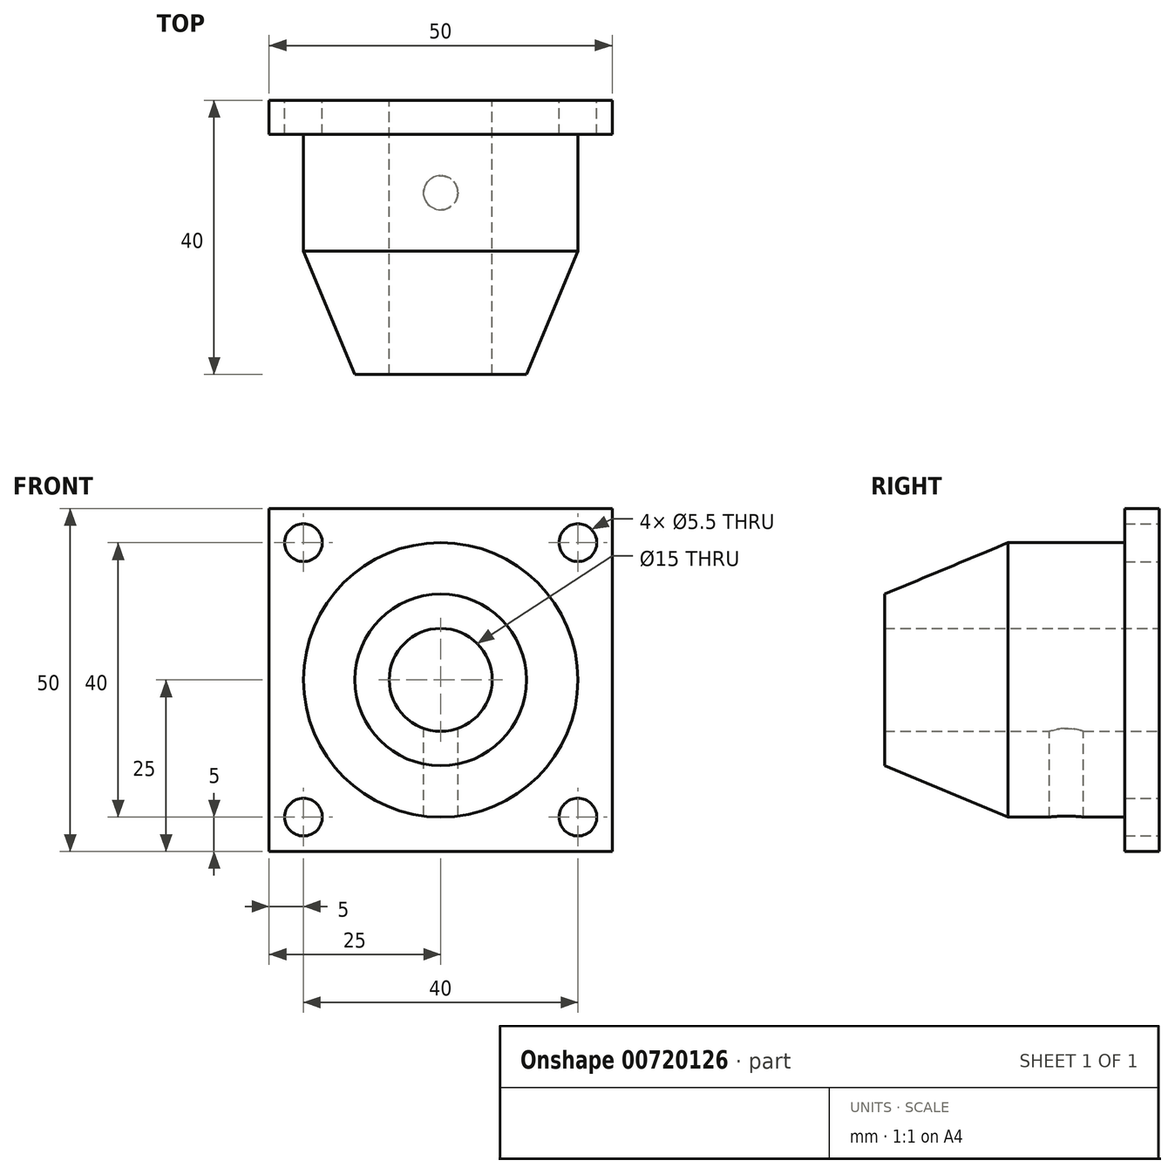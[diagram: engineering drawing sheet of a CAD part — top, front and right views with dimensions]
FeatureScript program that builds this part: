
annotation { "Feature Type Name" : "Feature", "Feature Type Description" : "" }
export const myFeature = defineFeature(function(context is Context, id is Id, definition is map)
    precondition{}
    {
        {
            var Q0;
            Q0=qCreatedBy(makeId("Front.planeOp"),FACE);
            var sketch = newSketch(context, id + "F0", { "sketchPlane" : qUnion([Q0])});
            skLineSegment(sketch, "E0.bottom", {"start": v(0, 0) * mm, "end": v(50, 0) * mm});
            skLineSegment(sketch, "E0.top", {"start": v(0, 50) * mm, "end": v(50, 50) * mm});
            skLineSegment(sketch, "E0.left", {"start": v(0, 0) * mm, "end": v(0, 50) * mm});
            skLineSegment(sketch, "E0.right", {"start": v(50, 0) * mm, "end": v(50, 50) * mm});
            skCircle(sketch, "E1", {"center": v(5, 45) * mm, "radius": 2.75 * mm});
            skCircle(sketch, "E2.0.1.0", {"center": v(5, 5) * mm, "radius": 2.75 * mm});
            skCircle(sketch, "E2.1.0.0", {"center": v(45, 45) * mm, "radius": 2.75 * mm});
            skCircle(sketch, "E2.1.1.0", {"center": v(45, 5) * mm, "radius": 2.75 * mm});
            skLineSegment(sketch, "E2.direction1", {"start": v(5, 45) * mm, "end": v(45, 45) * mm, "construction": true});
            skLineSegment(sketch, "E2.direction2", {"start": v(5, 45) * mm, "end": v(5, 5) * mm, "construction": true});
            skSolve(sketch);
        }
        {
            var Q0;
            Q0=makeQuery(id+"F0.imprint","IMPRINT",FACE,{"disambiguationData":[TD([[makeQuery(id+"F0.imprint","IMPRINT",EDGE,{"derivedFrom":sQuery(id+"F0.wireOp",EDGE,"E0.bottom")}),1.0]])]});
            extrude(context, id + "F1", {"entities" : qUnion([Q0]), "depth" : 5 * mm, "offsetDistance" : 25 * mm});
        }
        {
            var Q0;
            Q0=makeQuery(id+"F1.opExtrude","CAP_FACE",FACE,{"disambiguationData":[OSD([sQuery(id+"F0.wireOp",EDGE,"E0.bottom"),sQuery(id+"F0.wireOp",EDGE,"E0.top"),sQuery(id+"F0.wireOp",EDGE,"E0.left"),sQuery(id+"F0.wireOp",EDGE,"E0.right"),sQuery(id+"F0.wireOp",EDGE,"E1"),sQuery(id+"F0.wireOp",EDGE,"E2.0.1.0"),sQuery(id+"F0.wireOp",EDGE,"E2.1.0.0"),sQuery(id+"F0.wireOp",EDGE,"E2.1.1.0")])],"isStart":false});
            var sketch = newSketch(context, id + "F2", { "sketchPlane" : qUnion([Q0])});
            skCircle(sketch, "E3", {"center": v(25, 25) * mm, "radius": 20 * mm});
            skPoint(sketch, "E3.centerSnap0", {"position": v(50, 25) * mm});
            skPoint(sketch, "E3.centerSnap1", {"position": v(25, 50) * mm});
            skSolve(sketch);
        }
        {
            var Q0;
            Q0=makeQuery(id+"F2.imprint","IMPRINT",FACE,{"disambiguationData":[TD([[makeQuery(id+"F2.imprint","IMPRINT",EDGE,{"derivedFrom":sQuery(id+"F2.wireOp",EDGE,"E3")}),1.0]])]});
            extrude(context, id + "F3", {"entities" : qUnion([Q0]), "operationType" : NewBodyOperationType.ADD, "depth" : 17 * mm, "offsetDistance" : 25 * mm});
        }
        {
            var Q0;
            Q0=qCreatedBy(makeId("Top.planeOp"),FACE);
            cPlane(context, id + "F4", {"entities" : qUnion([Q0]), "cplaneType" : CPlaneType.OFFSET, "offset" : 25 * mm, "width" : 150 * mm, "height" : 150 * mm});
        }
        {
            var Q0;
            Q0=qCreatedBy(id+"F4.planeOp",FACE);
            var sketch = newSketch(context, id + "F5", { "sketchPlane" : qUnion([Q0])});
            skLineSegment(sketch, "E4", {"start": v(25, -22) * mm, "end": v(25, -40) * mm});
            skLineSegment(sketch, "E5", {"start": v(17.5, -40) * mm, "end": v(12.5, -40) * mm});
            skLineSegment(sketch, "E6", {"start": v(12.5, -40) * mm, "end": v(5, -22) * mm});
            skLineSegment(sketch, "E7", {"start": v(17.5, -22) * mm, "end": v(5, -22) * mm});
            skLineSegment(sketch, "E8.0", {"start": v(17.5, -22) * mm, "end": v(17.5, -40) * mm});
            skSolve(sketch);
        }
        {
            var Q0;
            Q0=makeQuery(id+"F5.imprint","IMPRINT",FACE,{"disambiguationData":[TD([[makeQuery(id+"F5.imprint","IMPRINT",EDGE,{"derivedFrom":sQuery(id+"F5.wireOp",EDGE,"E5")}),-1.0]])]});
            var Q1;
            Q1=sQuery(id+"F5.wireOp",EDGE,"E4");
            revolve(context, id + "F6", {"operationType" : NewBodyOperationType.ADD, "surfaceOperationType" : NewSurfaceOperationType.NEW, "entities" : qUnion([Q0]), "axis" : qUnion([Q1]), "revolveType" : RevolveType.FULL});
        }
        {
            var Q0;
            Q0=makeQuery(id+"F1.opExtrude","CAP_FACE",FACE,{"disambiguationData":[OSD([sQuery(id+"F0.wireOp",EDGE,"E0.bottom"),sQuery(id+"F0.wireOp",EDGE,"E0.top"),sQuery(id+"F0.wireOp",EDGE,"E0.left"),sQuery(id+"F0.wireOp",EDGE,"E0.right"),sQuery(id+"F0.wireOp",EDGE,"E1"),sQuery(id+"F0.wireOp",EDGE,"E2.0.1.0"),sQuery(id+"F0.wireOp",EDGE,"E2.1.0.0"),sQuery(id+"F0.wireOp",EDGE,"E2.1.1.0")])],"isStart":true});
            var sketch = newSketch(context, id + "F7", { "sketchPlane" : qUnion([Q0])});
            skCircle(sketch, "E9", {"center": v(-25, 25) * mm, "radius": 7.5 * mm});
            skPoint(sketch, "E9.centerSnap0", {"position": v(0, 25) * mm});
            skPoint(sketch, "E9.centerSnap1", {"position": v(-25, 50) * mm});
            skSolve(sketch);
        }
        {
            var Q0;
            Q0=makeQuery(id+"F7.imprint","IMPRINT",FACE,{"disambiguationData":[TD([[makeQuery(id+"F7.imprint","IMPRINT",EDGE,{"derivedFrom":sQuery(id+"F7.wireOp",EDGE,"E9")}),1.0]])]});
            extrude(context, id + "F8", {"entities" : qUnion([Q0]), "operationType" : NewBodyOperationType.REMOVE, "endBound" : BoundingType.THROUGH_ALL, "oppositeDirection" : true, "depth" : 25 * mm, "offsetDistance" : 25 * mm});
        }
        {
            var Q0;
            Q0=qCreatedBy(id+"F4.planeOp",FACE);
            var sketch = newSketch(context, id + "F9", { "sketchPlane" : qUnion([Q0])});
            skCircle(sketch, "E10", {"center": v(25, -13.5) * mm, "radius": 2.5 * mm});
            skSolve(sketch);
        }
        {
            var Q0;
            Q0 = qSketchRegion(id + "F9", true);
            extrude(context, id + "F10", {"entities" : qUnion([Q0]), "operationType" : NewBodyOperationType.REMOVE, "endBound" : BoundingType.THROUGH_ALL, "oppositeDirection" : true, "depth" : 25 * mm, "offsetDistance" : 25 * mm});
        }
    });
